# Revit family: 94895214
name_source: partatom
category: Modelos genéricos
units: mm (PartAtom-declared; Revit-internal decimal feet)

## family parameters
Com base no plano de trabalho = Não
Compartilhado = Não
Corte com vazios quando carregada = Não
Cota do conector redondo = Utilizar diâmetro
Pode hospedar o vergalhão = Não
Ponto de cálculo do ambiente = Não
Sempre na vertical = Sim
Tipo de parte = Normal

## types (1)
- 94895214
    Acabamento = Scotch Brite
    Descrição = Lava-Louças
    Dimensões = 845,5 x 600 x 600 mm (Profundidade)
    Elevação padrão = 0 mm  [stored 0 ft]
    Fabricante = Tramontina
    Material predominante = Aço Inox
    Modelo = Lava-Louças Tramontina SB14X 60
    Referência do produto = 94895/214
    Tipo de material = AISI 430
    URL da ficha técnica = https://assets.tramontina.com.br
    URL do fabricante = tramontina.com.br
    URL do produto = https://www.tramontina.com.br
    URL dos arquivos BIM = tramontina.com.br/biblioteca

note: [stored X ft] marks values corroborated as IEEE doubles in the binary element streams (Revit-internal decimal feet)
